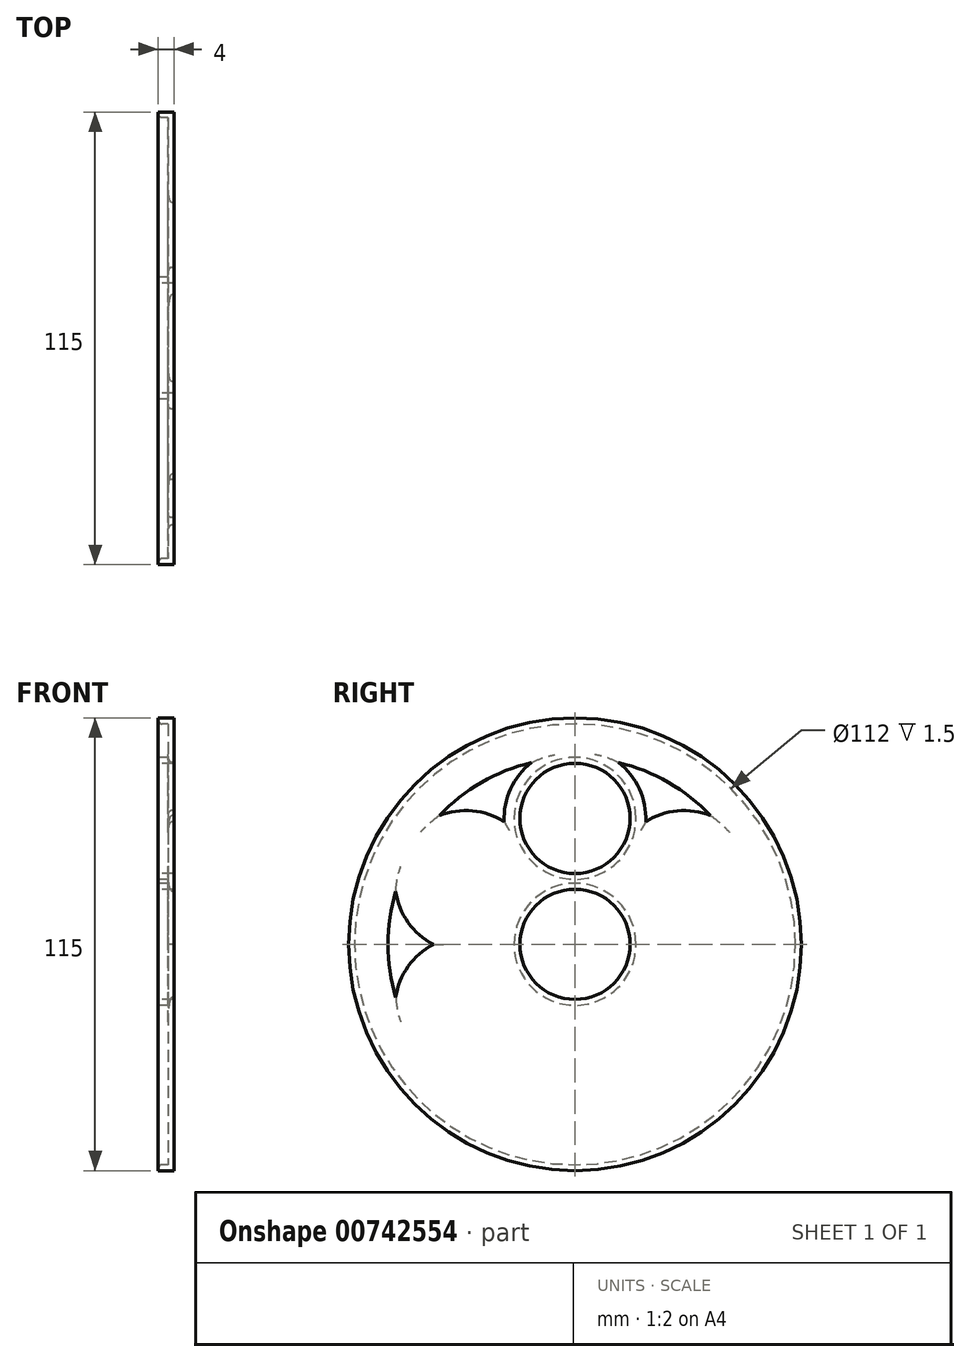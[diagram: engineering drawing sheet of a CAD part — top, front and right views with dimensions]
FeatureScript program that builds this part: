
annotation { "Feature Type Name" : "Feature", "Feature Type Description" : "" }
export const myFeature = defineFeature(function(context is Context, id is Id, definition is map)
    precondition{}
    {
        {
            var Q0;
            Q0=qCreatedBy(makeId("Front.planeOp"),FACE);
            var sketch = newSketch(context, id + "F0", { "sketchPlane" : qUnion([Q0])});
            skLineSegment(sketch, "E0.bottom", {"start": v(0, 0) * mm, "end": v(4, 0) * mm});
            skLineSegment(sketch, "E0.top", {"start": v(0, 57.5) * mm, "end": v(4, 57.5) * mm});
            skLineSegment(sketch, "E0.left", {"start": v(0, 0) * mm, "end": v(0, 57.5) * mm});
            skLineSegment(sketch, "E0.right", {"start": v(4, 0) * mm, "end": v(4, 57.5) * mm});
            skSolve(sketch);
        }
        {
            var Q0;
            Q0=makeQuery(id+"F0.imprint","IMPRINT",FACE,{"disambiguationData":[TD([[makeQuery(id+"F0.imprint","IMPRINT",EDGE,{"derivedFrom":sQuery(id+"F0.wireOp",EDGE,"E0.bottom")}),1.0]])]});
            var Q1;
            Q1=sQuery(id+"F0.wireOp",EDGE,"E0.bottom");
            revolve(context, id + "F1", {"surfaceOperationType" : NewSurfaceOperationType.NEW, "entities" : qUnion([Q0]), "axis" : qUnion([Q1]), "revolveType" : RevolveType.FULL});
        }
        {
            var Q0;
            Q0=qCreatedBy(makeId("Right.planeOp"),FACE);
            var sketch = newSketch(context, id + "F2", { "sketchPlane" : qUnion([Q0])});
            skPoint(sketch, "E1", {"position": v(0, 0) * mm});
            skSolve(sketch);
        }
        {
            var Q0;
            Q0=sQuery(id+"F2.wireOp",VERTEX,"E1");
            var Q1;
            Q1=makeQuery(id+"F1.opRevolve","SWEPT_BODY",BODY,{"disambiguationData":[OSD([sQuery(id+"F0.wireOp",EDGE,"E0.bottom"),sQuery(id+"F0.wireOp",EDGE,"E0.top"),sQuery(id+"F0.wireOp",EDGE,"E0.left"),sQuery(id+"F0.wireOp",EDGE,"E0.right")])]});
            hole(context, id + "F3", {"style" : HoleStyle.SIMPLE, "endStyle" : HoleEndStyle.BLIND, "oppositeDirection" : true, "holeDiameter" : 28 * mm, "majorDiameter" : 5 * mm, "holeDepth" : 10 * mm, "isTappedThrough" : true, "tappedDepth" : 12 * mm, "tapClearance" : 3, "locations" : qUnion([Q0]), "scope" : qUnion([Q1])});
        }
        {
            var Q0;
            Q0=qCreatedBy(makeId("Right.planeOp"),FACE);
            var sketch = newSketch(context, id + "F4", { "sketchPlane" : qUnion([Q0])});
            skPoint(sketch, "E2", {"position": v(0, 0) * mm});
            skPoint(sketch, "E3", {"position": v(0, 32) * mm});
            skSolve(sketch);
        }
        {
            var Q0;
            Q0=sQuery(id+"F4.wireOp",VERTEX,"E3");
            var Q1;
            Q1=makeQuery(id+"F1.opRevolve","SWEPT_BODY",BODY,{"disambiguationData":[OSD([sQuery(id+"F0.wireOp",EDGE,"E0.bottom"),sQuery(id+"F0.wireOp",EDGE,"E0.top"),sQuery(id+"F0.wireOp",EDGE,"E0.left"),sQuery(id+"F0.wireOp",EDGE,"E0.right")])]});
            hole(context, id + "F5", {"style" : HoleStyle.SIMPLE, "endStyle" : HoleEndStyle.BLIND, "oppositeDirection" : true, "holeDiameter" : 28 * mm, "majorDiameter" : 5 * mm, "holeDepth" : 10 * mm, "isTappedThrough" : true, "tappedDepth" : 12 * mm, "tapClearance" : 3, "locations" : qUnion([Q0]), "scope" : qUnion([Q1])});
        }
        {
            var Q0;
            Q0=makeQuery(id+"F1.opRevolve","SWEPT_FACE",FACE,{"disambiguationData":[OSD([sQuery(id+"F0.wireOp",EDGE,"E0.left")])]});
            shell(context, id + "F6", {"entities" : qUnion([Q0]), "thickness" : 1.5 * mm});
        }
        {
            var Q0;
            Q0=qCreatedBy(makeId("Right.planeOp"),FACE);
            var sketch = newSketch(context, id + "F7", { "sketchPlane" : qUnion([Q0])});
            skLineSegment(sketch, "E4", {"start": v(57.7, -33.32) * mm, "end": v(-56.61, 32.69) * mm});
            skLineSegment(sketch, "E5", {"start": v(56.26, 32.48) * mm, "end": v(-56.14, -32.41) * mm});
            skLineSegment(sketch, "E6", {"start": v(0, 63.52) * mm, "end": v(0, -67.12) * mm});
            skPoint(sketch, "E7", {"position": v(27.71, 16) * mm});
            skPoint(sketch, "E8", {"position": v(0, 32) * mm});
            skPoint(sketch, "E9", {"position": v(-27.71, 16) * mm});
            skPoint(sketch, "E10", {"position": v(27.71, -16) * mm});
            skPoint(sketch, "E11", {"position": v(0, -32) * mm});
            skPoint(sketch, "E12", {"position": v(-27.71, -16) * mm});
            skArc(sketch, "E13", {"start": v(34.47, 32.68) * mm, "mid": v(26.04, 33.92) * mm, "end": v(17.98, 31.14) * mm});
            skArc(sketch, "E14", {"start": v(17.98, 31.14) * mm, "mid": v(16.36, 39.5) * mm, "end": v(11.07, 46.2) * mm});
            skArc(sketch, "E15", {"start": v(-11.07, 46.2) * mm, "mid": v(-16.36, 39.5) * mm, "end": v(-17.98, 31.14) * mm});
            skArc(sketch, "E16", {"start": v(-17.98, 31.14) * mm, "mid": v(-26.04, 33.92) * mm, "end": v(-34.47, 32.68) * mm});
            skArc(sketch, "E17", {"start": v(45.54, 13.5) * mm, "mid": v(42.4, 5.59) * mm, "end": v(35.96, 0) * mm});
            skArc(sketch, "E18", {"start": v(35.96, 0) * mm, "mid": v(42.4, -5.59) * mm, "end": v(45.54, -13.5) * mm});
            skArc(sketch, "E19", {"start": v(-45.54, 13.5) * mm, "mid": v(-42.4, 5.59) * mm, "end": v(-35.96, 0) * mm});
            skArc(sketch, "E20", {"start": v(-45.54, -13.5) * mm, "mid": v(-42.4, -5.59) * mm, "end": v(-35.96, 0) * mm});
            skArc(sketch, "E21", {"start": v(34.47, -32.68) * mm, "mid": v(26.04, -33.92) * mm, "end": v(17.98, -31.14) * mm});
            skArc(sketch, "E22", {"start": v(11.07, -46.2) * mm, "mid": v(16.36, -39.5) * mm, "end": v(17.98, -31.14) * mm});
            skArc(sketch, "E23", {"start": v(-11.07, -46.2) * mm, "mid": v(-16.36, -39.5) * mm, "end": v(-17.98, -31.14) * mm});
            skArc(sketch, "E24", {"start": v(-34.47, -32.68) * mm, "mid": v(-26.04, -33.92) * mm, "end": v(-17.98, -31.14) * mm});
            skArc(sketch, "E25", {"start": v(34.47, 32.68) * mm, "mid": v(23.75, 41.14) * mm, "end": v(11.07, 46.2) * mm});
            skArc(sketch, "E26", {"start": v(-11.07, 46.2) * mm, "mid": v(-23.75, 41.14) * mm, "end": v(-34.47, 32.68) * mm});
            skArc(sketch, "E27", {"start": v(-45.54, 13.5) * mm, "mid": v(-47.5, 0) * mm, "end": v(-45.54, -13.5) * mm});
            skArc(sketch, "E28", {"start": v(45.54, 13.5) * mm, "mid": v(47.5, 0) * mm, "end": v(45.54, -13.5) * mm});
            skArc(sketch, "E29", {"start": v(34.47, -32.68) * mm, "mid": v(23.75, -41.14) * mm, "end": v(11.07, -46.2) * mm});
            skArc(sketch, "E30", {"start": v(-11.07, -46.2) * mm, "mid": v(-23.75, -41.14) * mm, "end": v(-34.47, -32.68) * mm});
            skCircle(sketch, "E31", {"center": v(27.71, 16) * mm, "radius": 10.95 * mm});
            skCircle(sketch, "E32", {"center": v(27.71, 16) * mm, "radius": 7.5 * mm});
            skCircle(sketch, "E33", {"center": v(27.71, 16) * mm, "radius": 5 * mm});
            skSolve(sketch);
        }
        {
            var Q0;
            Q0=makeQuery(id+"F7.imprint","IMPRINT",FACE,{"disambiguationData":[TD([[makeQuery(id+"F7.imprint","IMPRINT",EDGE,{"derivedFrom":sQuery(id+"F7.wireOp",EDGE,"E15")}),-1.0]])]});
            var Q1;
            Q1=makeQuery(id+"F7.imprint","IMPRINT",FACE,{"disambiguationData":[TD([[makeQuery(id+"F7.imprint","IMPRINT",EDGE,{"derivedFrom":sQuery(id+"F7.wireOp",EDGE,"E13")}),-1.0]])]});
            var Q2;
            Q2=makeQuery(id+"F7.imprint","IMPRINT",FACE,{"disambiguationData":[TD([[makeQuery(id+"F7.imprint","IMPRINT",EDGE,{"derivedFrom":sQuery(id+"F7.wireOp",EDGE,"E17")}),1.0]])]});
            var Q3;
            Q3=makeQuery(id+"F7.imprint","IMPRINT",FACE,{"disambiguationData":[TD([[makeQuery(id+"F7.imprint","IMPRINT",EDGE,{"derivedFrom":sQuery(id+"F7.wireOp",EDGE,"E21")}),1.0]])]});
            var Q4;
            Q4=makeQuery(id+"F7.imprint","IMPRINT",FACE,{"disambiguationData":[TD([[makeQuery(id+"F7.imprint","IMPRINT",EDGE,{"derivedFrom":sQuery(id+"F7.wireOp",EDGE,"E23")}),1.0]])]});
            var Q5;
            Q5=makeQuery(id+"F7.imprint","IMPRINT",FACE,{"disambiguationData":[TD([[makeQuery(id+"F7.imprint","IMPRINT",EDGE,{"derivedFrom":sQuery(id+"F7.wireOp",EDGE,"E19")}),-1.0]])]});
            extrude(context, id + "F8", {"entities" : qUnion([Q0, Q1, Q2, Q3, Q4, Q5]), "operationType" : NewBodyOperationType.REMOVE, "depth" : 25 * mm, "offsetDistance" : 25 * mm});
        }
        {
            var Q0;
            Q0=makeQuery(id+"F8.boolean.opBoolean","INTERSECT",EDGE,{"derivedFrom":[makeQuery(id+"F6.opShell","OFFSET_FACE",FACE,{"disambiguationData":[OSD([sQuery(id+"F0.wireOp",EDGE,"E0.right")])]}),makeQuery(id+"F8.opExtrude","SWEPT_FACE",FACE,{"disambiguationData":[OSD([sQuery(id+"F7.wireOp",EDGE,"E28")])]})]});
            var Q1;
            Q1=makeQuery(id+"F8.boolean.opBoolean","INTERSECT",EDGE,{"derivedFrom":[makeQuery(id+"F6.opShell","OFFSET_FACE",FACE,{"disambiguationData":[OSD([sQuery(id+"F0.wireOp",EDGE,"E0.right")])]}),makeQuery(id+"F8.opExtrude","SWEPT_FACE",FACE,{"disambiguationData":[OSD([sQuery(id+"F7.wireOp",EDGE,"E17")])]})]});
            var Q2;
            Q2=makeQuery(id+"F8.boolean.opBoolean","INTERSECT",EDGE,{"derivedFrom":[makeQuery(id+"F6.opShell","OFFSET_FACE",FACE,{"disambiguationData":[OSD([sQuery(id+"F0.wireOp",EDGE,"E0.right")])]}),makeQuery(id+"F8.opExtrude","SWEPT_FACE",FACE,{"disambiguationData":[OSD([sQuery(id+"F7.wireOp",EDGE,"E18")])]})]});
            var Q3;
            Q3=makeQuery(id+"F8.boolean.opBoolean","INTERSECT",EDGE,{"derivedFrom":[makeQuery(id+"F6.opShell","OFFSET_FACE",FACE,{"disambiguationData":[OSD([sQuery(id+"F0.wireOp",EDGE,"E0.right")])]}),makeQuery(id+"F8.opExtrude","SWEPT_FACE",FACE,{"disambiguationData":[OSD([sQuery(id+"F7.wireOp",EDGE,"E25")])]})]});
            var Q4;
            Q4=makeQuery(id+"F8.boolean.opBoolean","INTERSECT",EDGE,{"derivedFrom":[makeQuery(id+"F6.opShell","OFFSET_FACE",FACE,{"disambiguationData":[OSD([sQuery(id+"F0.wireOp",EDGE,"E0.right")])]}),makeQuery(id+"F8.opExtrude","SWEPT_FACE",FACE,{"disambiguationData":[OSD([sQuery(id+"F7.wireOp",EDGE,"E13")])]})]});
            var Q5;
            Q5=makeQuery(id+"F8.boolean.opBoolean","INTERSECT",EDGE,{"derivedFrom":[makeQuery(id+"F6.opShell","OFFSET_FACE",FACE,{"disambiguationData":[OSD([sQuery(id+"F0.wireOp",EDGE,"E0.right")])]}),makeQuery(id+"F8.opExtrude","SWEPT_FACE",FACE,{"disambiguationData":[OSD([sQuery(id+"F7.wireOp",EDGE,"E14")])]})]});
            var Q6;
            Q6=makeQuery(id+"F8.boolean.opBoolean","INTERSECT",EDGE,{"derivedFrom":[makeQuery(id+"F6.opShell","OFFSET_FACE",FACE,{"disambiguationData":[OSD([sQuery(id+"F0.wireOp",EDGE,"E0.right")])]}),makeQuery(id+"F8.opExtrude","SWEPT_FACE",FACE,{"disambiguationData":[OSD([sQuery(id+"F7.wireOp",EDGE,"E15")])]})]});
            var Q7;
            Q7=makeQuery(id+"F8.boolean.opBoolean","INTERSECT",EDGE,{"derivedFrom":[makeQuery(id+"F6.opShell","OFFSET_FACE",FACE,{"disambiguationData":[OSD([sQuery(id+"F0.wireOp",EDGE,"E0.right")])]}),makeQuery(id+"F8.opExtrude","SWEPT_FACE",FACE,{"disambiguationData":[OSD([sQuery(id+"F7.wireOp",EDGE,"E26")])]})]});
            var Q8;
            Q8=makeQuery(id+"F8.boolean.opBoolean","INTERSECT",EDGE,{"derivedFrom":[makeQuery(id+"F6.opShell","OFFSET_FACE",FACE,{"disambiguationData":[OSD([sQuery(id+"F0.wireOp",EDGE,"E0.right")])]}),makeQuery(id+"F8.opExtrude","SWEPT_FACE",FACE,{"disambiguationData":[OSD([sQuery(id+"F7.wireOp",EDGE,"E16")])]})]});
            var Q9;
            Q9=makeQuery(id+"F8.boolean.opBoolean","INTERSECT",EDGE,{"derivedFrom":[makeQuery(id+"F6.opShell","OFFSET_FACE",FACE,{"disambiguationData":[OSD([sQuery(id+"F0.wireOp",EDGE,"E0.right")])]}),makeQuery(id+"F8.opExtrude","SWEPT_FACE",FACE,{"disambiguationData":[OSD([sQuery(id+"F7.wireOp",EDGE,"E27")])]})]});
            var Q10;
            Q10=makeQuery(id+"F8.boolean.opBoolean","INTERSECT",EDGE,{"derivedFrom":[makeQuery(id+"F6.opShell","OFFSET_FACE",FACE,{"disambiguationData":[OSD([sQuery(id+"F0.wireOp",EDGE,"E0.right")])]}),makeQuery(id+"F8.opExtrude","SWEPT_FACE",FACE,{"disambiguationData":[OSD([sQuery(id+"F7.wireOp",EDGE,"E19")])]})]});
            var Q11;
            Q11=makeQuery(id+"F8.boolean.opBoolean","INTERSECT",EDGE,{"derivedFrom":[makeQuery(id+"F6.opShell","OFFSET_FACE",FACE,{"disambiguationData":[OSD([sQuery(id+"F0.wireOp",EDGE,"E0.right")])]}),makeQuery(id+"F8.opExtrude","SWEPT_FACE",FACE,{"disambiguationData":[OSD([sQuery(id+"F7.wireOp",EDGE,"E20")])]})]});
            var Q12;
            Q12=makeQuery(id+"F8.boolean.opBoolean","INTERSECT",EDGE,{"derivedFrom":[makeQuery(id+"F6.opShell","OFFSET_FACE",FACE,{"disambiguationData":[OSD([sQuery(id+"F0.wireOp",EDGE,"E0.right")])]}),makeQuery(id+"F8.opExtrude","SWEPT_FACE",FACE,{"disambiguationData":[OSD([sQuery(id+"F7.wireOp",EDGE,"E30")])]})]});
            var Q13;
            Q13=makeQuery(id+"F8.boolean.opBoolean","INTERSECT",EDGE,{"derivedFrom":[makeQuery(id+"F6.opShell","OFFSET_FACE",FACE,{"disambiguationData":[OSD([sQuery(id+"F0.wireOp",EDGE,"E0.right")])]}),makeQuery(id+"F8.opExtrude","SWEPT_FACE",FACE,{"disambiguationData":[OSD([sQuery(id+"F7.wireOp",EDGE,"E24")])]})]});
            var Q14;
            Q14=makeQuery(id+"F8.boolean.opBoolean","INTERSECT",EDGE,{"derivedFrom":[makeQuery(id+"F6.opShell","OFFSET_FACE",FACE,{"disambiguationData":[OSD([sQuery(id+"F0.wireOp",EDGE,"E0.right")])]}),makeQuery(id+"F8.opExtrude","SWEPT_FACE",FACE,{"disambiguationData":[OSD([sQuery(id+"F7.wireOp",EDGE,"E23")])]})]});
            var Q15;
            Q15=makeQuery(id+"F8.boolean.opBoolean","INTERSECT",EDGE,{"derivedFrom":[makeQuery(id+"F6.opShell","OFFSET_FACE",FACE,{"disambiguationData":[OSD([sQuery(id+"F0.wireOp",EDGE,"E0.right")])]}),makeQuery(id+"F8.opExtrude","SWEPT_FACE",FACE,{"disambiguationData":[OSD([sQuery(id+"F7.wireOp",EDGE,"E22")])]})]});
            var Q16;
            Q16=makeQuery(id+"F8.boolean.opBoolean","INTERSECT",EDGE,{"derivedFrom":[makeQuery(id+"F6.opShell","OFFSET_FACE",FACE,{"disambiguationData":[OSD([sQuery(id+"F0.wireOp",EDGE,"E0.right")])]}),makeQuery(id+"F8.opExtrude","SWEPT_FACE",FACE,{"disambiguationData":[OSD([sQuery(id+"F7.wireOp",EDGE,"E29")])]})]});
            var Q17;
            Q17=makeQuery(id+"F8.boolean.opBoolean","INTERSECT",EDGE,{"derivedFrom":[makeQuery(id+"F6.opShell","OFFSET_FACE",FACE,{"disambiguationData":[OSD([sQuery(id+"F0.wireOp",EDGE,"E0.right")])]}),makeQuery(id+"F8.opExtrude","SWEPT_FACE",FACE,{"disambiguationData":[OSD([sQuery(id+"F7.wireOp",EDGE,"E21")])]})]});
            var Q18;
            Q18=makeQuery(id+"F6.opShell","OFFSET_EDGE",EDGE,{"disambiguationData":[OSD([sQuery(id+"F0.wireOp",EDGE,"E0.top"),sQuery(id+"F0.wireOp",EDGE,"E0.left")])]});
            fillet(context, id + "F9", {"entities" : qUnion([Q0, Q1, Q2, Q3, Q4, Q5, Q6, Q7, Q8, Q9, Q10, Q11, Q12, Q13, Q14, Q15, Q16, Q17, Q18]), "radius" : 1 * mm, "tangentPropagation" : true, "allowEdgeOverflow" : false});
        }
    });
